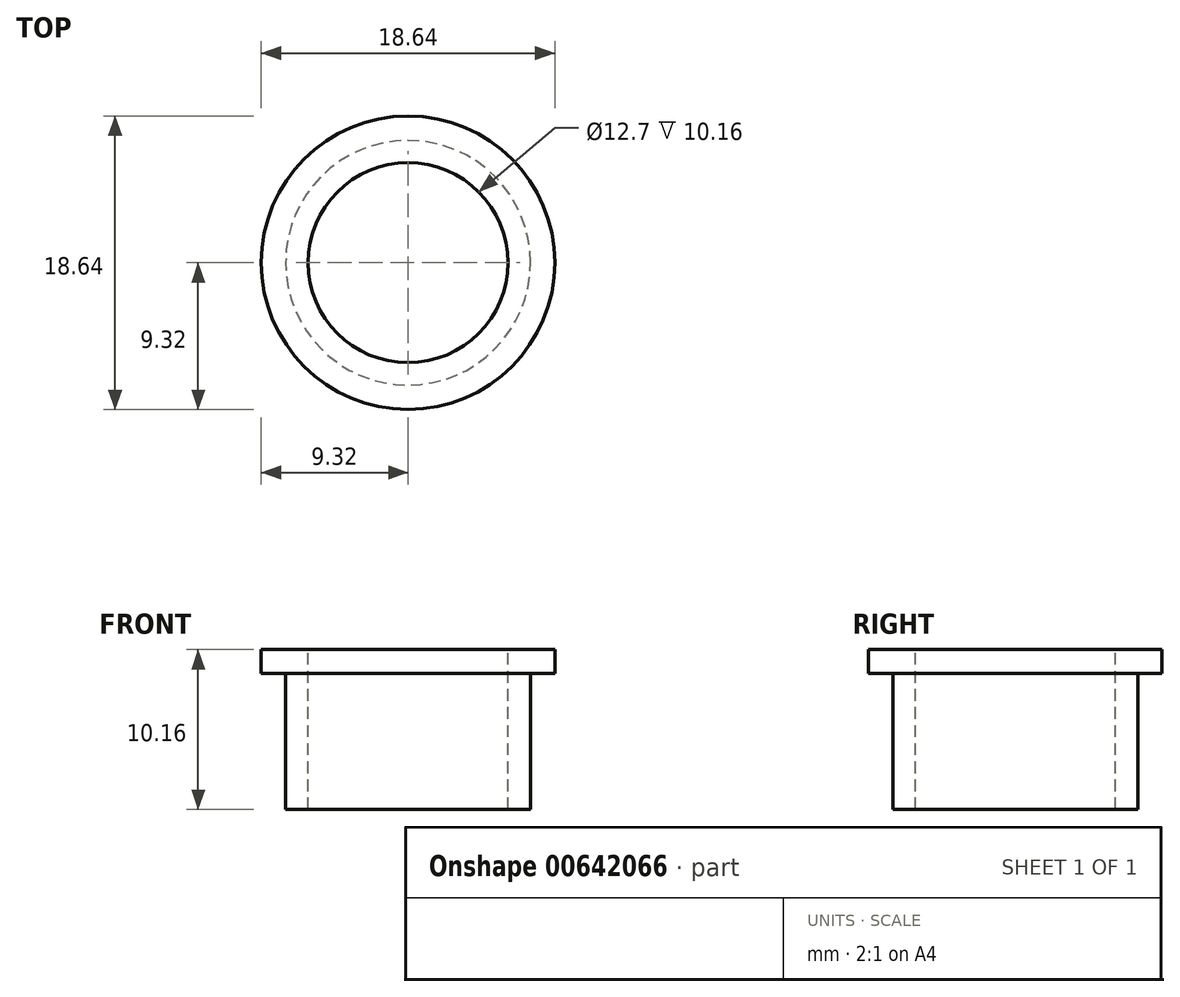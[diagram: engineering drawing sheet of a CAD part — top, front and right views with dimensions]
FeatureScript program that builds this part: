
annotation { "Feature Type Name" : "Feature", "Feature Type Description" : "" }
export const myFeature = defineFeature(function(context is Context, id is Id, definition is map)
    precondition{}
    {
        {
            var Q0;
            Q0=qCreatedBy(makeId("Top.planeOp"),FACE);
            var sketch = newSketch(context, id + "F0", { "sketchPlane" : qUnion([Q0])});
            skCircle(sketch, "E0", {"center": v(0, 0) * mm, "radius": 9.32 * mm});
            skSolve(sketch);
        }
        {
            var Q0;
            Q0 = qSketchRegion(id + "F0", true);
            extrude(context, id + "F1", {"entities" : qUnion([Q0]), "depth" : 1.52 * mm, "offsetDistance" : 25.4 * mm});
        }
        {
            var Q0;
            Q0=makeQuery(id+"F1.opExtrude","CAP_FACE",FACE,{"disambiguationData":[OSD([sQuery(id+"F0.wireOp",EDGE,"E0")])],"isStart":true});
            var sketch = newSketch(context, id + "F2", { "sketchPlane" : qUnion([Q0])});
            skCircle(sketch, "E1", {"center": v(0, 0) * mm, "radius": 7.77 * mm});
            skSolve(sketch);
        }
        {
            var Q0;
            Q0 = qSketchRegion(id + "F2", true);
            extrude(context, id + "F3", {"entities" : qUnion([Q0]), "operationType" : NewBodyOperationType.ADD, "depth" : 8.64 * mm, "offsetDistance" : 25.4 * mm});
        }
        {
            var Q0;
            Q0=makeQuery(id+"F1.opExtrude","CAP_FACE",FACE,{"disambiguationData":[OSD([sQuery(id+"F0.wireOp",EDGE,"E0")])],"isStart":false});
            var sketch = newSketch(context, id + "F4", { "sketchPlane" : qUnion([Q0])});
            skCircle(sketch, "E2", {"center": v(0, 0) * mm, "radius": 6.35 * mm});
            skSolve(sketch);
        }
        {
            var Q0;
            Q0 = qSketchRegion(id + "F4", true);
            extrude(context, id + "F5", {"entities" : qUnion([Q0]), "operationType" : NewBodyOperationType.REMOVE, "endBound" : BoundingType.THROUGH_ALL, "oppositeDirection" : true, "depth" : 25.4 * mm, "offsetDistance" : 25.4 * mm});
        }
    });
